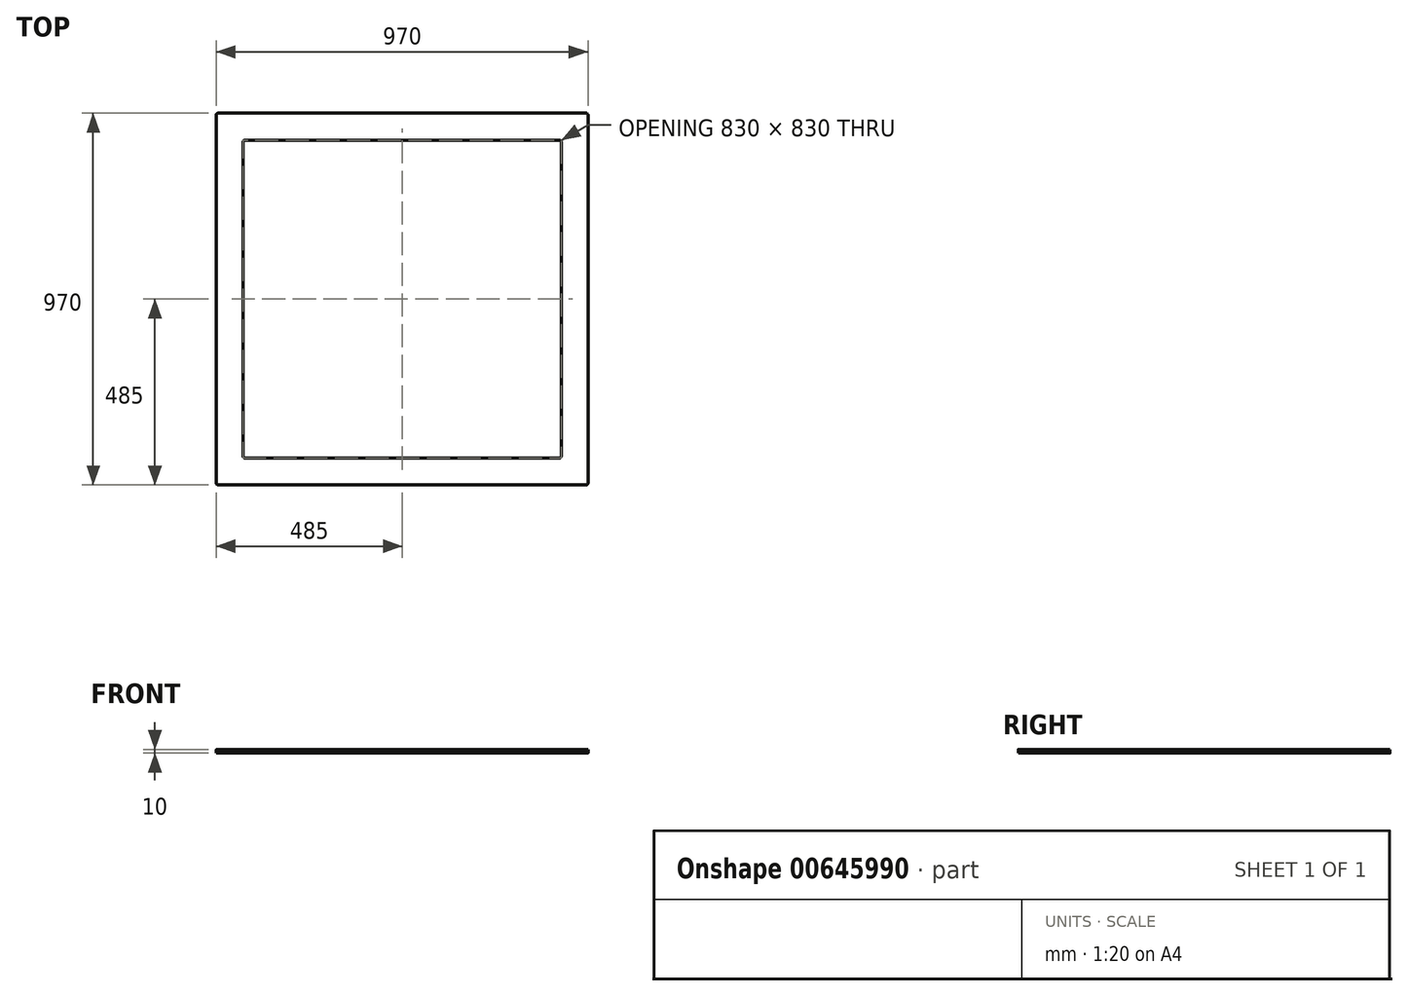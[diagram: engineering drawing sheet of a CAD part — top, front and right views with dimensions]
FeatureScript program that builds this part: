
annotation { "Feature Type Name" : "Feature", "Feature Type Description" : "" }
export const myFeature = defineFeature(function(context is Context, id is Id, definition is map)
    precondition{}
    {
        {
            var Q0;
            Q0=qCreatedBy(makeId("Top.planeOp"),FACE);
            var sketch = newSketch(context, id + "F0", { "sketchPlane" : qUnion([Q0])});
            skLineSegment(sketch, "E0.bottom", {"start": v(485, 485) * mm, "end": v(-485, 485) * mm});
            skLineSegment(sketch, "E0.top", {"start": v(485, -485) * mm, "end": v(-485, -485) * mm});
            skLineSegment(sketch, "E0.left", {"start": v(485, 485) * mm, "end": v(485, -485) * mm});
            skLineSegment(sketch, "E0.right", {"start": v(-485, 485) * mm, "end": v(-485, -485) * mm});
            skPoint(sketch, "E0.middle", {"position": v(0, 0) * mm});
            skLineSegment(sketch, "E1.bottom", {"start": v(415, 415) * mm, "end": v(-415, 415) * mm});
            skLineSegment(sketch, "E1.top", {"start": v(415, -415) * mm, "end": v(-415, -415) * mm});
            skLineSegment(sketch, "E1.left", {"start": v(415, 415) * mm, "end": v(415, -415) * mm});
            skLineSegment(sketch, "E1.right", {"start": v(-415, 415) * mm, "end": v(-415, -415) * mm});
            skSolve(sketch);
        }
        {
            var Q0;
            Q0=makeQuery(id+"F0.imprint","IMPRINT",FACE,{"disambiguationData":[TD([[makeQuery(id+"F0.imprint","IMPRINT",EDGE,{"derivedFrom":sQuery(id+"F0.wireOp",EDGE,"E0.bottom")}),1.0]])]});
            extrude(context, id + "F1", {"entities" : qUnion([Q0]), "depth" : 10 * mm, "offsetDistance" : 25 * mm});
        }
        {
            var Q0;
            Q0=makeQuery(id+"F1.opExtrude","SWEPT_EDGE",EDGE,{"disambiguationData":[OSD([sQuery(id+"F0.wireOp",EDGE,"E1.bottom"),sQuery(id+"F0.wireOp",EDGE,"E1.right")])]});
            var Q1;
            Q1=makeQuery(id+"F1.opExtrude","SWEPT_EDGE",EDGE,{"disambiguationData":[OSD([sQuery(id+"F0.wireOp",EDGE,"E1.bottom"),sQuery(id+"F0.wireOp",EDGE,"E1.left")])]});
            var Q2;
            Q2=makeQuery(id+"F1.opExtrude","SWEPT_EDGE",EDGE,{"disambiguationData":[OSD([sQuery(id+"F0.wireOp",EDGE,"E1.top"),sQuery(id+"F0.wireOp",EDGE,"E1.left")])]});
            var Q3;
            Q3=makeQuery(id+"F1.opExtrude","SWEPT_EDGE",EDGE,{"disambiguationData":[OSD([sQuery(id+"F0.wireOp",EDGE,"E1.top"),sQuery(id+"F0.wireOp",EDGE,"E1.right")])]});
            var Q4;
            Q4=makeQuery(id+"F1.opExtrude","SWEPT_EDGE",EDGE,{"disambiguationData":[OSD([sQuery(id+"F0.wireOp",EDGE,"E0.top"),sQuery(id+"F0.wireOp",EDGE,"E0.right")])]});
            var Q5;
            Q5=makeQuery(id+"F1.opExtrude","SWEPT_EDGE",EDGE,{"disambiguationData":[OSD([sQuery(id+"F0.wireOp",EDGE,"E0.top"),sQuery(id+"F0.wireOp",EDGE,"E0.left")])]});
            var Q6;
            Q6=makeQuery(id+"F1.opExtrude","SWEPT_EDGE",EDGE,{"disambiguationData":[OSD([sQuery(id+"F0.wireOp",EDGE,"E0.bottom"),sQuery(id+"F0.wireOp",EDGE,"E0.right")])]});
            var Q7;
            Q7=makeQuery(id+"F1.opExtrude","SWEPT_EDGE",EDGE,{"disambiguationData":[OSD([sQuery(id+"F0.wireOp",EDGE,"E0.bottom"),sQuery(id+"F0.wireOp",EDGE,"E0.left")])]});
            fillet(context, id + "F2", {"entities" : qUnion([Q0, Q1, Q2, Q3, Q4, Q5, Q6, Q7]), "radius" : 5 * mm, "tangentPropagation" : true, "allowEdgeOverflow" : false});
        }
    });
